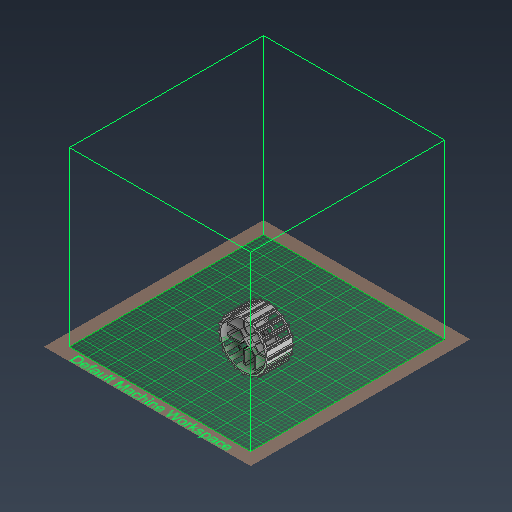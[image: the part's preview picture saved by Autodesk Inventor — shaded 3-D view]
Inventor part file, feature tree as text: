
AUTODESK INVENTOR PART (.ipt)
format: ipt  version: 2021 (Build 250183000, 183)  size: 1,160,192 bytes
history: native  units: mm
features: extrude x6, other x4, pattern_circular x2, sketch x2, plane x1, hole x1
ambient origin geometry x8: Origin, YZ Plane, XZ Plane, XY Plane, X Axis, Y Axis, Z Axis, Center Point
bodies: Volumenkörper1 (feature_tree)
feature tree (16):
  other  "Grundskizze"
  extrude  "Außenrahmen"  Depth=3.0mm
  extrude  "Radnabe"  Depth=2.0mm
  other  "Profilskizze"
  extrude  "Streben"  TaperAngle=45.0deg  [1 undecoded]
  extrude  "Profil"  TaperAngle=135.0deg  [1 undecoded]
  pattern_circular  "Runde Anordnung1"  [2 undecoded]
  other  "Einpresssmutter_skizze"
  other  "Einpressmutter_skizze2"
  plane  "Arbeitsebene2"
  extrude  "Extrusion13"  Depth=2.0mm
  pattern_circular  "Runde Anordnung4"  [2 undecoded]
  extrude  "Extrusion14"  Depth=35.0mm TaperAngle=0.0deg
  hole  "Bohrung1"  [1 undecoded]
  sketch  "Skizze9"  dims[d0=110.0mm d1=3.0mm]
  sketch  "Skizze10"  dims[d2=9.0mm d7=15.0mm d8=45.0deg d10=135.0deg d11=3.0mm d12=3.0mm d17=45.0mm d18=15.0mm d19=0.0mm d20=0.0mm d21=35.0mm d22=0.0mm d50=40.0mm d52=360.0deg d54=30.0mm d55=0.0mm d58=0.5mm d59=60.0mm d60=0.0mm d61=200.0mm d62=360.0deg d64=4.0mm d65=3.0mm d71=4.5mm d72=7.119163mm d75=4.5mm d78=1.5mm d79=2.5mm d88=5.0mm d89=40.0mm d91=360.0deg d93=7.118079mm d107=25.0mm d108=7.5mm d109=25.0mm d110=7.5mm d111=3.5mm d112=3.5mm d113=20.0mm d115=17.0mm d116=10.0mm d118=10.0mm d120=20.0mm d122=17.0mm d123=10.0mm d125=10.0mm d127=16.0mm d128=0.0mm d129=40.0mm d130=360.0deg d132=5.3mm d133=0.6mm d134=25.0mm d135=0.0mm d136=4.0mm d137=6.0mm d138=4.0mm d139=2.0mm d140=90.0deg d141=8.0mm d142=20.594885mm d73=0.5mm d74=0.872665mm]
note: 7 required parameter values undecoded (feature->parameter linkage not recoverable at this tier; creation-order binding heuristic only, values carry confidence <= 0.55)
